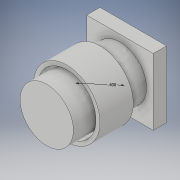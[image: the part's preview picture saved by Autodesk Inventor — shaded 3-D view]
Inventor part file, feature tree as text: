
AUTODESK INVENTOR PART (.ipt)
format: ipt  version: 2018 (Build 220112000, 112)  size: 127,488 bytes
history: native  units: in
note: dims shown in document units (in); Inventor stores cm internally (conversion verified against a paired STEP export)
features: extrude x4, sketch x3, plane x2
ambient origin geometry x8: Origin, YZ Plane, XZ Plane, XY Plane, X Axis, Y Axis, Z Axis, Center Point
bodies: Solid1 (feature_tree)
feature tree (9):
  sketch  "Sketch1"  dims[d0=0.4in d1=0.4in d2=0.0in]
  extrude  "Extrusion1"  Depth=0.4in TaperAngle=0.0deg
  plane  "Work Plane1"
  extrude  "Extrusion4"  Depth=0.5in
  extrude  "Extrusion5"  Depth=0.15in TaperAngle=0.0deg
  extrude  "Extrusion6"  Depth=0.5in
  plane  "Work Plane2"
  sketch  "Sketch4"  dims[d13=0.44in d14=0.5in]
  sketch  "Sketch5"  dims[d15=0.25in d16=0.0in d17=0.15in d18=0.0in d19=0.5in d20=0.5in d21=0.25in d22=0.25in d23=0.1in d24=0.0in]
